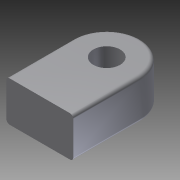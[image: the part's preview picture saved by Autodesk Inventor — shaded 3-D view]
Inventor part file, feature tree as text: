
AUTODESK INVENTOR PART (.ipt)
format: ipt  version: 2011 SP2 (Build 150309200, 309)  size: 101,376 bytes
history: native  units: mm
features: extrude x1, fillet x1, sketch x1
ambient origin geometry x8: Origin, YZ Plane, XZ Plane, XY Plane, X Axis, Y Axis, Z Axis, Center Point
bodies: Solid1 (feature_tree)
feature tree (3):
  extrude  "Extrusion1"  Depth=60.0mm
  fillet  "Fillet1"  Radius=8.0mm
  sketch  "Sketch1"  dims[d0=40.0mm d1=60.0mm d2=8.0mm d3=24.0mm d4=0.0mm d5=2.0mm]
